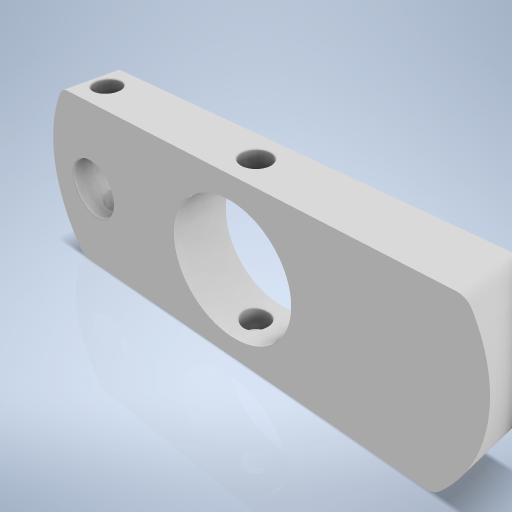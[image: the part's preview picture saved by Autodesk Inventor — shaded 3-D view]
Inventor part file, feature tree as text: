
AUTODESK INVENTOR PART (.ipt)
format: ipt  version: 2024.2 (Build 282272000, 272)  size: 270,848 bytes
history: native  units: mm
features: hole x4, sketch x3, extrude x1
ambient origin geometry x8: Origin, YZ Plane, XZ Plane, XY Plane, X Axis, Y Axis, Z Axis, Center Point
bodies: Volumenkörper1 (feature_tree)
feature tree (8):
  extrude  "Extrusion1"  Depth=48.0mm
  sketch  "Skizze2"  dims[d3=0.0mm d5=16.0mm d6=0.0mm]
  hole  "Bohrung1"  [1 undecoded]
  hole  "Bohrung2"  [1 undecoded]
  sketch  "Skizze3"  dims[d7=36.0mm d8=6.0mm d9=4.0mm d10=2.0mm d11=90.0deg d12=8.0mm d13=20.594885mm d17=16.0mm d18=6.0mm d19=4.0mm d20=2.0mm d21=90.0deg d22=8.0mm d23=20.594885mm d24=128.0mm d25=4.0mm d26=40.0mm d27=40.0mm d29=48.0mm d30=8.0mm d31=6.0mm d32=4.0mm d33=2.0mm d34=90.0deg d35=8.0mm d36=20.594885mm d37=8.0mm d38=8.0mm d39=6.0mm d40=4.0mm d41=2.0mm d42=90.0deg d43=8.0mm d44=20.594885mm]
  hole  "Bohrung3"  [1 undecoded]
  hole  "Bohrung4"  [1 undecoded]
  sketch  "Skizze1"  dims[d1=0.0mm d2=48.0mm]
note: 4 required parameter values undecoded (feature->parameter linkage not recoverable at this tier; creation-order binding heuristic only, values carry confidence <= 0.55)
